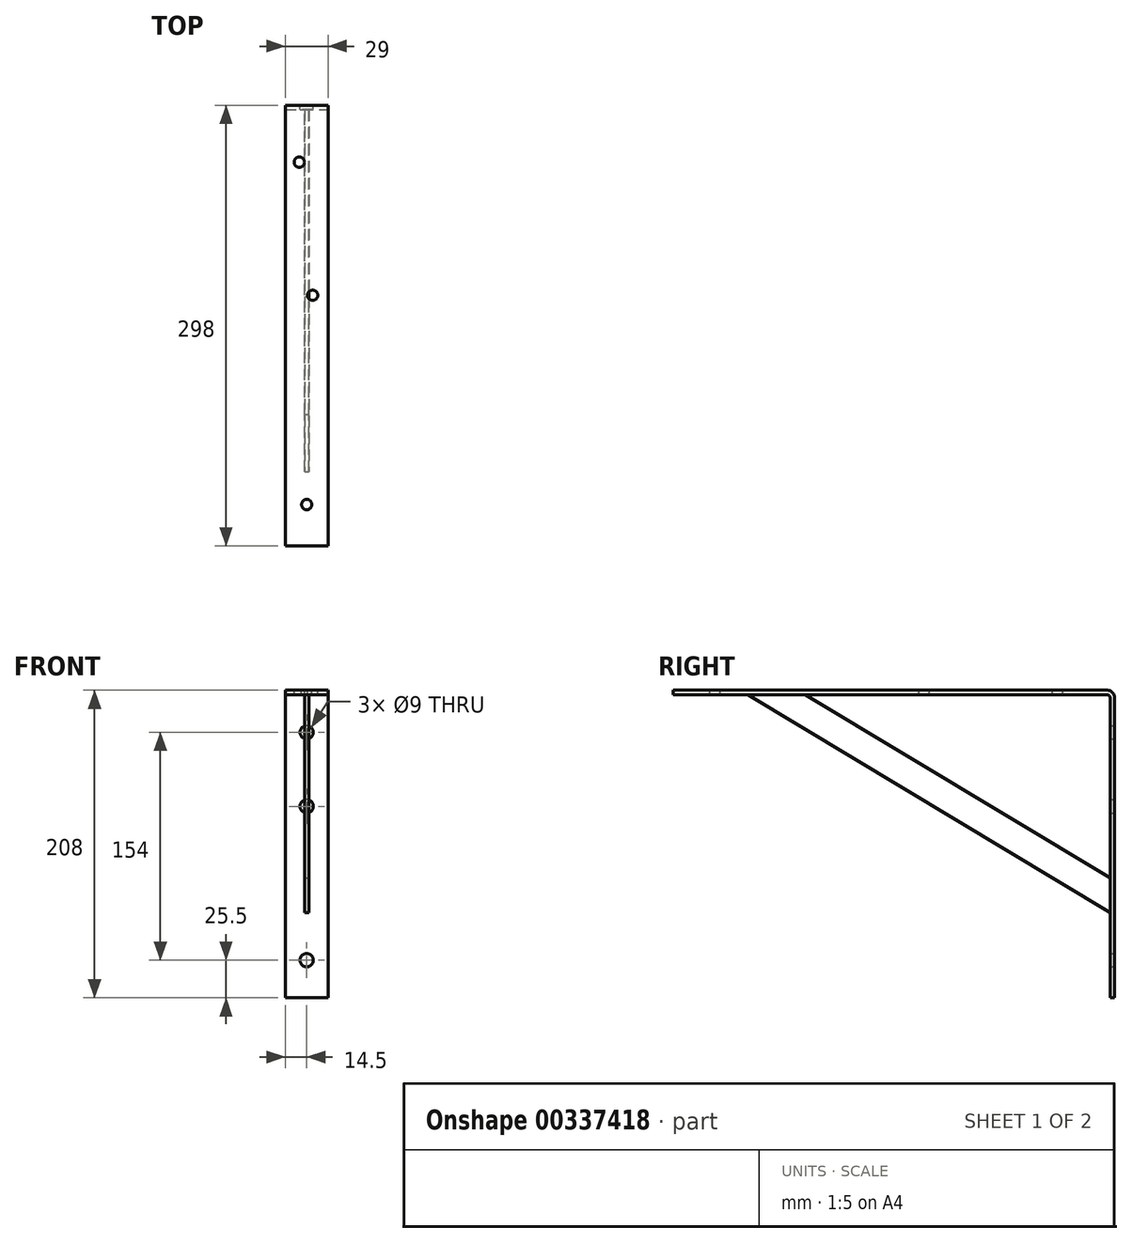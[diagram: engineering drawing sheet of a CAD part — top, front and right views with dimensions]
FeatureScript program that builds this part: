
annotation { "Feature Type Name" : "Feature", "Feature Type Description" : "" }
export const myFeature = defineFeature(function(context is Context, id is Id, definition is map)
    precondition{}
    {
        {
            var Q0;
            Q0=qCreatedBy(makeId("Right.planeOp"),FACE);
            var sketch = newSketch(context, id + "F0", { "sketchPlane" : qUnion([Q0])});
            skLineSegment(sketch, "E0", {"start": v(-298, 0) * mm, "end": v(-5, 0) * mm});
            skLineSegment(sketch, "E1", {"start": v(0, -5) * mm, "end": v(0, -208) * mm});
            skPoint(sketch, "E2.visualSharp", {"position": v(0, 0) * mm});
            skArc(sketch, "E2.filletArc", {"start": v(0, -5) * mm, "mid": v(-1.46, -1.46) * mm, "end": v(-5, 0) * mm});
            skLineSegment(sketch, "E3.0", {"start": v(-3, -5) * mm, "end": v(-3, -208) * mm});
            skLineSegment(sketch, "E3.1", {"start": v(-298, -3) * mm, "end": v(-5, -3) * mm});
            skPoint(sketch, "E4.visualSharp", {"position": v(-3, -3) * mm});
            skArc(sketch, "E4.filletArc", {"start": v(-3, -5) * mm, "mid": v(-3.59, -3.59) * mm, "end": v(-5, -3) * mm});
            skLineSegment(sketch, "E5", {"start": v(-3, -208) * mm, "end": v(0, -208) * mm});
            skLineSegment(sketch, "E6", {"start": v(-298, -3) * mm, "end": v(-298, 0) * mm});
            skSolve(sketch);
        }
        {
            var Q0;
            Q0=qSketchRegion(id+"F0",true);
            extrude(context, id + "F1", {"entities" : qUnion([Q0]), "endBound" : BoundingType.SYMMETRIC, "oppositeDirection" : true, "depth" : 29 * mm});
        }
        {
            var Q0;
            Q0=qCreatedBy(makeId("Right.planeOp"),FACE);
            var sketch = newSketch(context, id + "F2", { "sketchPlane" : qUnion([Q0])});
            skLineSegment(sketch, "E7", {"start": v(-3, -127) * mm, "end": v(-3, -150.34) * mm});
            skLineSegment(sketch, "E8", {"start": v(-3, -150.34) * mm, "end": v(-247.78, -3) * mm});
            skLineSegment(sketch, "E9", {"start": v(-247.78, -3) * mm, "end": v(-209, -3) * mm});
            skLineSegment(sketch, "E10", {"start": v(-209, -3) * mm, "end": v(-3, -127) * mm});
            skSolve(sketch);
        }
        {
            var Q0;
            Q0=qSketchRegion(id+"F2",true);
            extrude(context, id + "F3", {"entities" : qUnion([Q0]), "operationType" : NewBodyOperationType.ADD, "endBound" : BoundingType.SYMMETRIC, "oppositeDirection" : true, "depth" : 3 * mm});
        }
        {
            var Q0;
            Q0=makeQuery(id+"F1.opExtrude","SWEPT_FACE",FACE,{"disambiguationData":[OSD([sQuery(id+"F0.wireOp",EDGE,"E1")])]});
            var sketch = newSketch(context, id + "F4", { "sketchPlane" : qUnion([Q0])});
            skLineSegment(sketch, "E11", {"start": v(0, -208) * mm, "end": v(0, -5) * mm, "construction": true});
            skCircle(sketch, "E12", {"center": v(0, -28.5) * mm, "radius": 4.5 * mm});
            skCircle(sketch, "E13", {"center": v(0, -78.5) * mm, "radius": 4.5 * mm});
            skCircle(sketch, "E14", {"center": v(0, -182.5) * mm, "radius": 4.5 * mm});
            skSolve(sketch);
        }
        {
            var Q0;
            Q0=qSketchRegion(id+"F4",true);
            extrude(context, id + "F5", {"entities" : qUnion([Q0]), "operationType" : NewBodyOperationType.REMOVE, "oppositeDirection" : true, "depth" : 3 * mm});
        }
        {
            var Q0;
            Q0=makeQuery(id+"F1.opExtrude","SWEPT_FACE",FACE,{"disambiguationData":[OSD([sQuery(id+"F0.wireOp",EDGE,"E0")])]});
            var sketch = newSketch(context, id + "F6", { "sketchPlane" : qUnion([Q0])});
            skCircle(sketch, "E15", {"center": v(-5, -38.5) * mm, "radius": 3.5 * mm});
            skCircle(sketch, "E16", {"center": v(4, -128.5) * mm, "radius": 3.5 * mm});
            skCircle(sketch, "E17", {"center": v(0, -270) * mm, "radius": 3.5 * mm});
            skSolve(sketch);
        }
        {
            var Q0;
            Q0=qSketchRegion(id+"F6",true);
            extrude(context, id + "F7", {"entities" : qUnion([Q0]), "operationType" : NewBodyOperationType.REMOVE, "oppositeDirection" : true, "depth" : 3 * mm});
        }
    });
